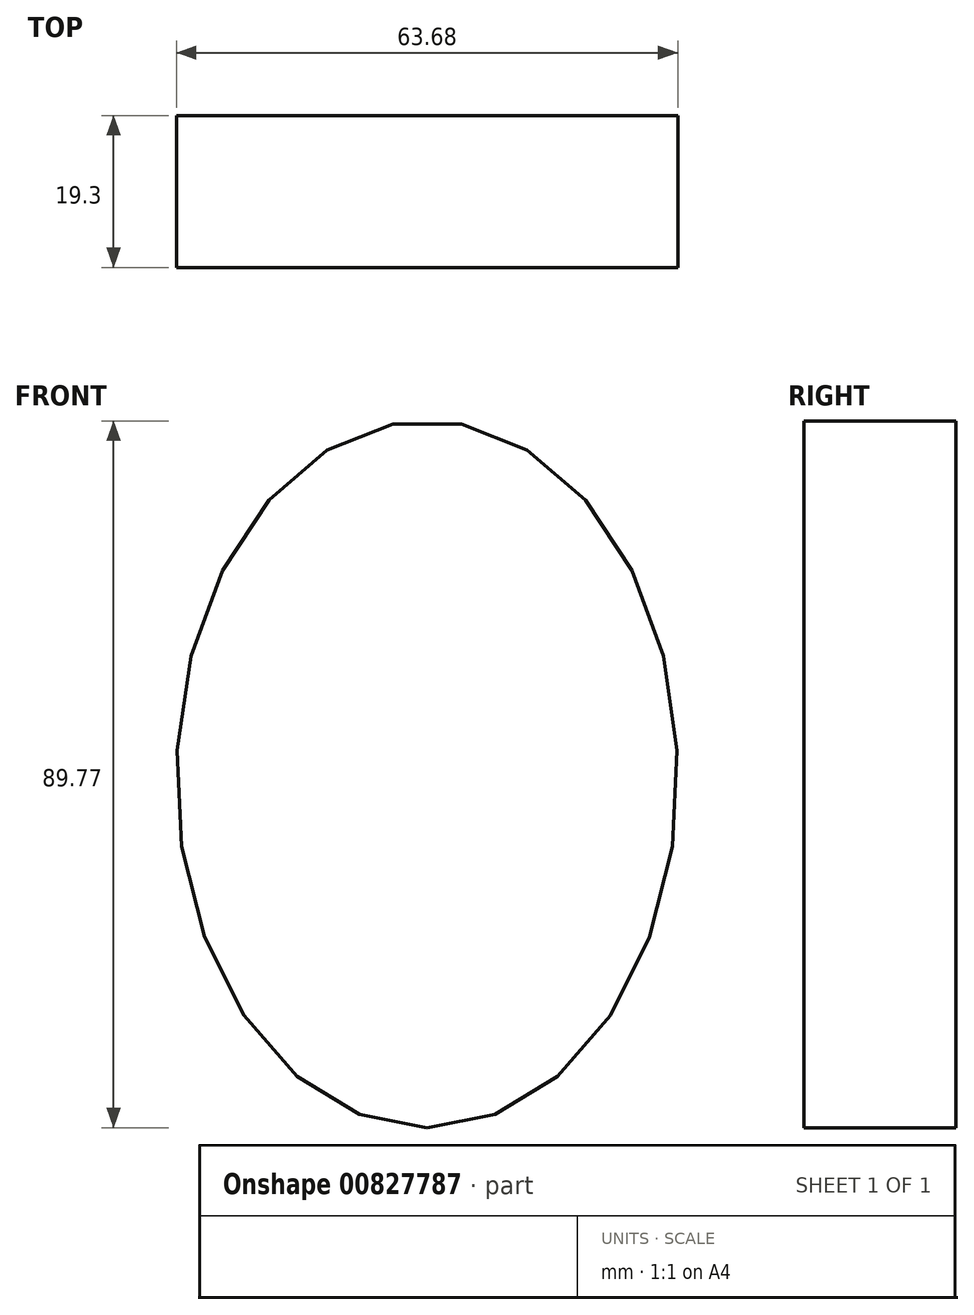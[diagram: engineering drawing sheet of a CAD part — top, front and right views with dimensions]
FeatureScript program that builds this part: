
annotation { "Feature Type Name" : "Feature", "Feature Type Description" : "" }
export const myFeature = defineFeature(function(context is Context, id is Id, definition is map)
    precondition{}
    {
        {
            var Q0;
            Q0=qCreatedBy(makeId("Front.planeOp"),FACE);
            var sketch = newSketch(context, id + "F0", { "sketchPlane" : qUnion([Q0])});
            skEllipse(sketch, "E0", {"center": v(-48.64, 44.44) * mm, "majorRadius": 44.88 * mm, "minorRadius": 31.84 * mm, "majorAxis": v(0, -1)});
            skSolve(sketch);
        }
        {
            var Q0;
            Q0=makeQuery(id+"F0.imprint","IMPRINT",FACE,{"disambiguationData":[TD([[makeQuery(id+"F0.imprint","IMPRINT",EDGE,{"derivedFrom":sQuery(id+"F0.wireOp",EDGE,"E0")}),1.0]])]});
            extrude(context, id + "F1", {"entities" : qUnion([Q0]), "depth" : 19.3 * mm, "offsetDistance" : 25.4 * mm});
        }
    });
